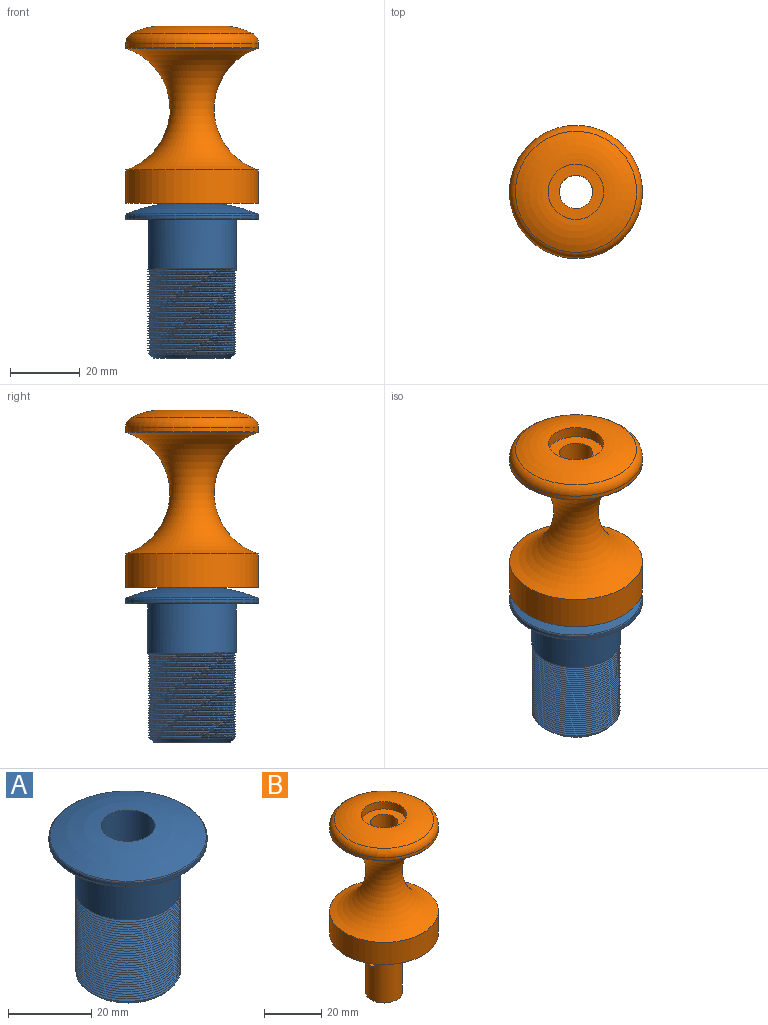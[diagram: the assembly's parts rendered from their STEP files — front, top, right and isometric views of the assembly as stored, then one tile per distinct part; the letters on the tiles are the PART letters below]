
ASSEMBLY  parts=2 mates=1
PART A: 13 faces, bbox 41.2x41.2x44.4 mm
  f0: cylinder r=12.7mm len=25.4mm, axis (0,0,1), area 1127.1mm2, adj f1,f6,f9
  f1: plane 37.34x37.34mm, normal (0,0,-1), area 588.2mm2, adj f0,f2
  f2: torus R=18.67mm, axis (0,0,1), area 71.1mm2, adj f1,f3
  f3: cylinder r=19.05mm len=38.1mm, axis (0,0,1), area 115.8mm2, adj f2,f4
  f4: torus R=18.67mm, axis (0,0,1), area 53.2mm2, adj f3,f5
  f5: torus R=2.71mm, axis (0,0,1), area 1020mm2, adj f4,f12
  f6: plane 0.76x0.7mm, normal (0,-1,0), area 0.3mm2, adj f0,f7,f8,f9
  f7: bspline ~29.12x25.21mm, area 1857.1mm2, adj f6,f8,f11
  f8: bspline ~29.12x25.21mm, area 1888.3mm2, adj f6,f7,f9,f11
  f9: bspline ~29.33x25.4mm, area 8.5mm2, adj f0,f6,f8
  f10: plane 22.35x22.35mm, normal (0,0,-1), area 259.3mm2, adj f11,f12
  f11: cone r=12.7mm half-angle=45deg, axis (0,0,1), area 117.6mm2, adj f7,f8,f10
  f12: cylinder r=6.51mm len=44.36mm, axis (0,0,1), area 1814.3mm2, adj f5,f10
PART B: 14 faces, bbox 53.5x53.5x76.2 mm
  f0: cylinder r=4.76mm len=73.03mm, axis (0,0,-1), area 2169.1mm2, adj f2,f10,f12,f13
  f1: torus R=8.55mm, axis (0,0,1), area 782.1mm2, adj f9,f11
  f2: plane 12.7x12.7mm, normal (0,0,-1), area 55.4mm2, adj f0,f3
  f3: cylinder r=6.35mm len=25.4mm, axis (0,0,1), area 997.5mm2, adj f2,f4,f12,f13
  f4: plane 38.1x38.1mm, normal (0,0,-1), area 1013.4mm2, adj f3,f5
  f5: cylinder r=19.05mm len=38.1mm, axis (0,0,1), area 1140.1mm2, adj f4,f6
  f6: torus R=24.71mm, axis (0,0,1), area 3116.8mm2, adj f5,f7
  f7: torus R=18.8mm, axis (0,0,1), area 37.8mm2, adj f6,f8
  f8: cylinder r=19.05mm len=38.1mm, axis (0,0,1), area 142.6mm2, adj f7,f9
  f9: torus R=15.88mm, axis (0,0,1), area 400mm2, adj f1,f8
  f10: plane 15.88x15.88mm, normal (0,0,1), area 126.7mm2, adj f0,f11
  f11: cylinder r=7.94mm len=15.88mm, axis (0,0,1), area 158.3mm2, adj f1,f10
  f12: cylinder r=1.59mm len=3.18mm, axis (1,0,0), area 16.2mm2, adj f0,f3
  f13: cylinder r=1.59mm len=3.18mm, axis (1,0,0), area 16.2mm2, adj f0,f3
PLACE A at identity fixed
PLACE B t=(0,0,48.17)mm
MATE slider B.f0 <-> A.f0  axis (0,0,1) through (0,0,19.7)mm
